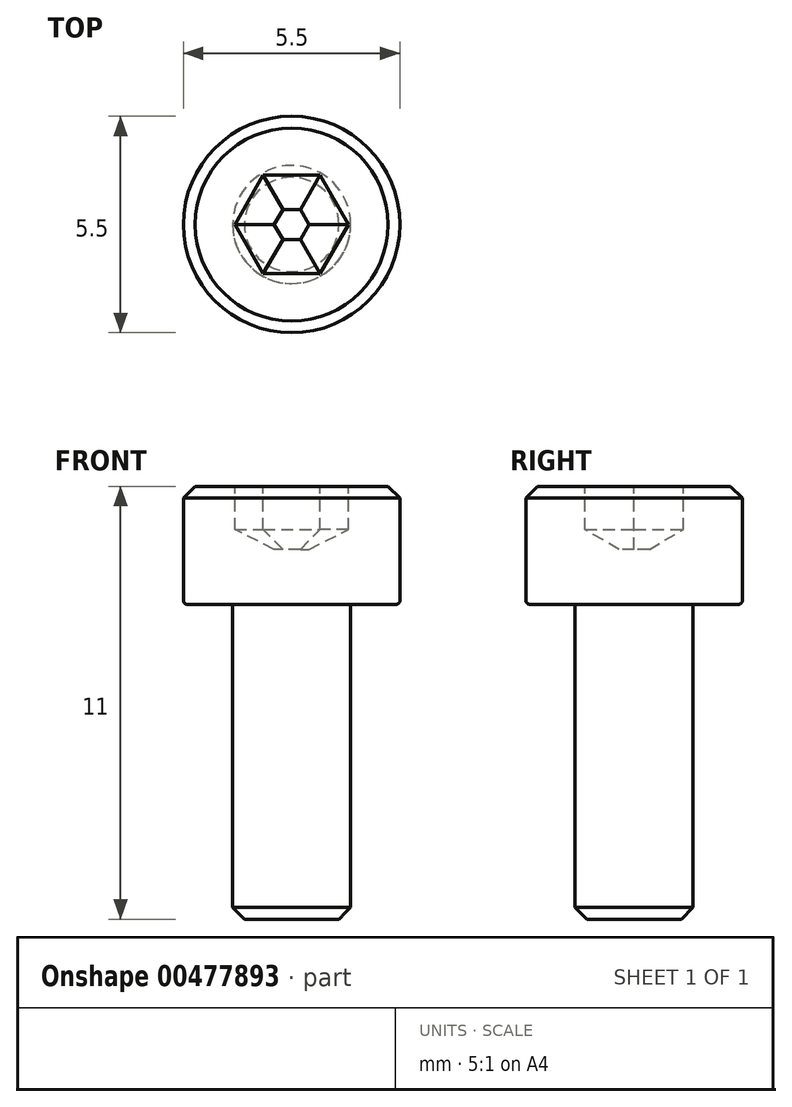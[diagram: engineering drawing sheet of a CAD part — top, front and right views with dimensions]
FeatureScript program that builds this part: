
annotation { "Feature Type Name" : "Feature", "Feature Type Description" : "" }
export const myFeature = defineFeature(function(context is Context, id is Id, definition is map)
    precondition{}
    {
        {
            var Q0;
            Q0=qCreatedBy(makeId("Front.planeOp"),FACE);
            var sketch = newSketch(context, id + "F0", { "sketchPlane" : qUnion([Q0])});
            skLineSegment(sketch, "E0", {"start": v(0, 0) * mm, "end": v(0, -13.37) * mm, "construction": true});
            skLineSegment(sketch, "E1", {"start": v(0, 0) * mm, "end": v(2.75, 0) * mm});
            skLineSegment(sketch, "E2", {"start": v(2.75, 0) * mm, "end": v(2.75, -3) * mm});
            skLineSegment(sketch, "E3", {"start": v(2.75, -3) * mm, "end": v(1.5, -3) * mm});
            skLineSegment(sketch, "E4", {"start": v(1.5, -3) * mm, "end": v(1.5, -11) * mm});
            skLineSegment(sketch, "E5", {"start": v(1.5, -11) * mm, "end": v(0, -11) * mm});
            skLineSegment(sketch, "E6", {"start": v(0, -11) * mm, "end": v(0, 0) * mm});
            skSolve(sketch);
        }
        {
            var Q0;
            Q0 = qSketchRegion(id + "F0", true);
            var Q1;
            Q1=sQuery(id+"F0.wireOp",EDGE,"E6");
            revolve(context, id + "F1", {"entities" : qUnion([Q0]), "axis" : qUnion([Q1]), "revolveType" : RevolveType.FULL});
        }
        {
            var Q0;
            Q0=makeQuery(id+"F1.opRevolve","SWEPT_FACE",FACE,{"disambiguationData":[OSD([sQuery(id+"F0.wireOp",EDGE,"E1")])]});
            var sketch = newSketch(context, id + "F2", { "sketchPlane" : qUnion([Q0])});
            skCircle(sketch, "E7.cCircle", {"center": v(0, 0) * mm, "radius": 1.25 * mm, "construction": true});
            skLineSegment(sketch, "E7.0", {"start": v(-0.72, 1.25) * mm, "end": v(0.72, 1.25) * mm});
            skLineSegment(sketch, "E7.1", {"start": v(0.72, 1.25) * mm, "end": v(1.44, 0) * mm});
            skLineSegment(sketch, "E7.2", {"start": v(1.44, 0) * mm, "end": v(0.72, -1.25) * mm});
            skLineSegment(sketch, "E7.3", {"start": v(0.72, -1.25) * mm, "end": v(-0.72, -1.25) * mm});
            skLineSegment(sketch, "E7.4", {"start": v(-0.72, -1.25) * mm, "end": v(-1.44, 0) * mm});
            skLineSegment(sketch, "E7.5", {"start": v(-1.44, 0) * mm, "end": v(-0.72, 1.25) * mm});
            skPoint(sketch, "E7.0.midPoint", {"position": v(0, 1.25) * mm});
            skSolve(sketch);
        }
        {
            var Q0;
            Q0=makeQuery(id+"F2.imprint","IMPRINT",FACE,{"disambiguationData":[TD([[makeQuery(id+"F2.imprint","IMPRINT",EDGE,{"derivedFrom":sQuery(id+"F2.wireOp",EDGE,"E7.0")}),-1.0]])]});
            extrude(context, id + "F3", {"entities" : qUnion([Q0]), "operationType" : NewBodyOperationType.REMOVE, "oppositeDirection" : true, "depth" : 1.6 * mm});
        }
        {
            var Q0;
            Q0=makeQuery(id+"F3.boolean.opBoolean","COPY",FACE,{"derivedFrom":makeQuery(id+"F3.opExtrude","CAP_FACE",FACE,{"disambiguationData":[OSD([sQuery(id+"F2.wireOp",EDGE,"E7.0"),sQuery(id+"F2.wireOp",EDGE,"E7.1"),sQuery(id+"F2.wireOp",EDGE,"E7.2"),sQuery(id+"F2.wireOp",EDGE,"E7.3"),sQuery(id+"F2.wireOp",EDGE,"E7.4"),sQuery(id+"F2.wireOp",EDGE,"E7.5")])],"isStart":false})});
            chamfer(context, id + "F4", {"entities" : qUnion([Q0]), "chamferType" : ChamferType.OFFSET_ANGLE, "width" : .5 * mm, "oppositeDirection" : false, "angle" : 60 * degree, "tangentPropagation" : true});
        }
        {
            var Q0;
            Q0=makeQuery(id+"F1.opRevolve","SWEPT_EDGE",EDGE,{"disambiguationData":[OSD([sQuery(id+"F0.wireOp",EDGE,"E1"),sQuery(id+"F0.wireOp",EDGE,"E2")])]});
            var Q1;
            Q1=makeQuery(id+"F1.opRevolve","SWEPT_EDGE",EDGE,{"disambiguationData":[OSD([sQuery(id+"F0.wireOp",EDGE,"E4"),sQuery(id+"F0.wireOp",EDGE,"E5")])]});
            chamfer(context, id + "F5", {"entities" : qUnion([Q0, Q1]), "width" : .3 * mm, "tangentPropagation" : true});
        }
        {
            var Q0;
            Q0=makeQuery(id+"F1.opRevolve","SWEPT_EDGE",EDGE,{"disambiguationData":[OSD([sQuery(id+"F0.wireOp",EDGE,"E2"),sQuery(id+"F0.wireOp",EDGE,"E3")])]});
            fillet(context, id + "F6", {"entities" : qUnion([Q0]), "radius" : .1 * mm, "tangentPropagation" : true, "allowEdgeOverflow" : false});
        }
        {
            var Q0;
            Q0=makeQuery(id+"F1.opRevolve","SWEPT_BODY",BODY,{"disambiguationData":[OSD([sQuery(id+"F0.wireOp",EDGE,"E1"),sQuery(id+"F0.wireOp",EDGE,"E2"),sQuery(id+"F0.wireOp",EDGE,"E3"),sQuery(id+"F0.wireOp",EDGE,"E4"),sQuery(id+"F0.wireOp",EDGE,"E5"),sQuery(id+"F0.wireOp",EDGE,"E6")])]});
            transform(context, id + "F7", {"entities" : qUnion([Q0]), "transformType" : TransformType.COPY});
        }
        {
            var Q0;
            Q0=makeQuery(id+"F7.opPattern","COPY",BODY,{"derivedFrom":makeQuery(id+"F1.opRevolve","SWEPT_BODY",BODY,{"disambiguationData":[OSD([sQuery(id+"F0.wireOp",EDGE,"E1"),sQuery(id+"F0.wireOp",EDGE,"E2"),sQuery(id+"F0.wireOp",EDGE,"E3"),sQuery(id+"F0.wireOp",EDGE,"E4"),sQuery(id+"F0.wireOp",EDGE,"E5"),sQuery(id+"F0.wireOp",EDGE,"E6")])]}),"instanceName":"1"});
            deleteBodies(context, id + "F8", {"entities" : qUnion([Q0])});
        }
    });
